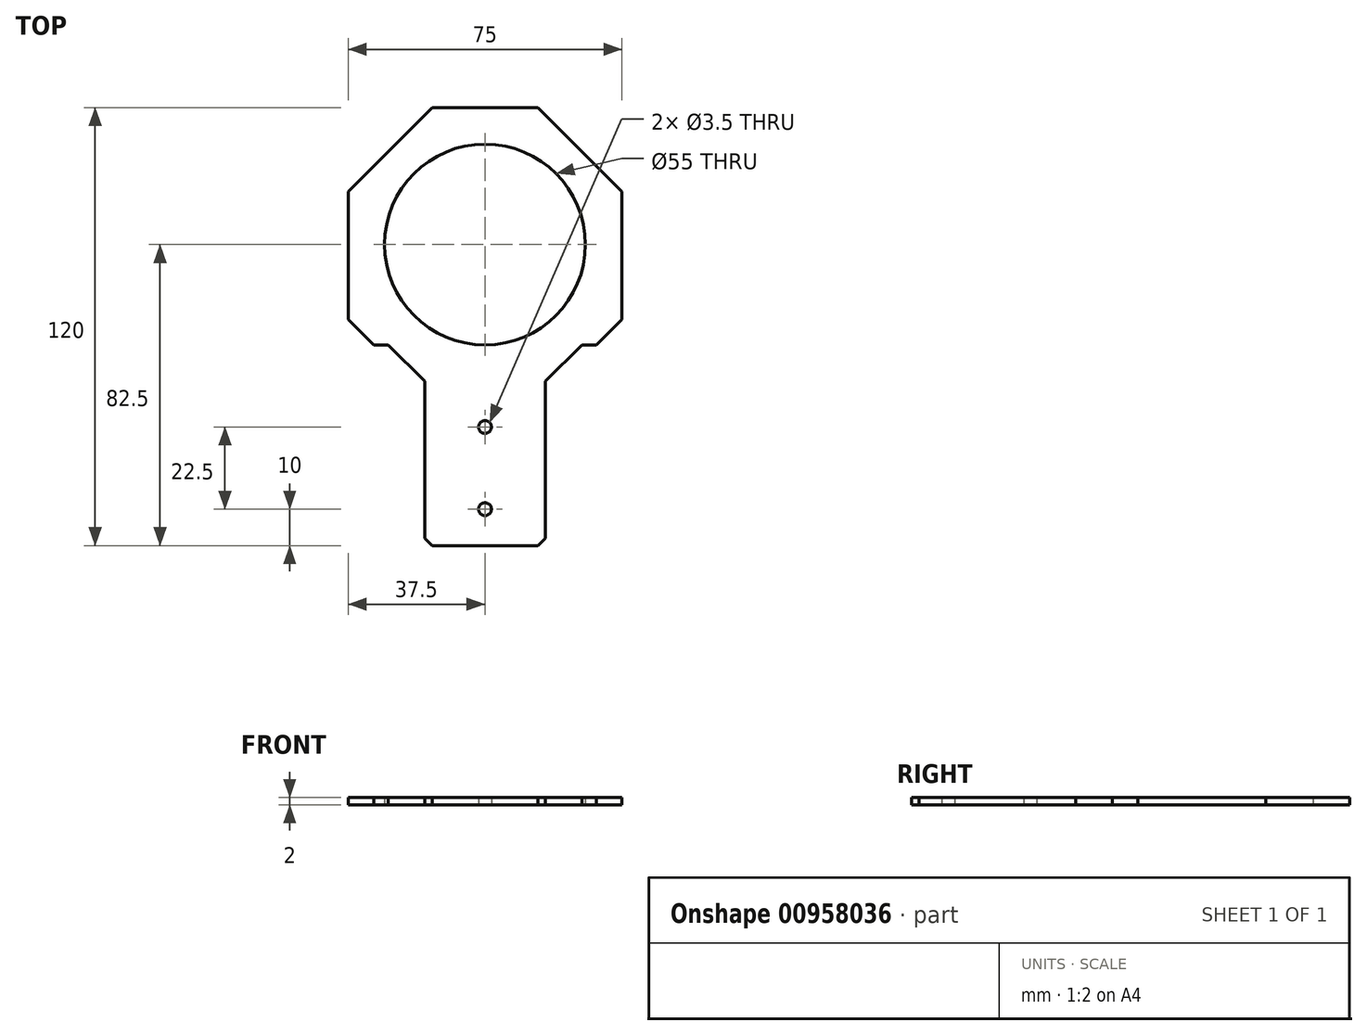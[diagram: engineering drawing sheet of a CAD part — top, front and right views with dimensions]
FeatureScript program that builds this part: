
annotation { "Feature Type Name" : "Feature", "Feature Type Description" : "" }
export const myFeature = defineFeature(function(context is Context, id is Id, definition is map)
    precondition{}
    {
        {
            var Q0;
            Q0=qCreatedBy(makeId("Top.planeOp"),FACE);
            var sketch = newSketch(context, id + "F0", { "sketchPlane" : qUnion([Q0])});
            skCircle(sketch, "E0", {"center": v(0, 0) * mm, "radius": 27.5 * mm});
            skLineSegment(sketch, "E1", {"start": v(0, 37.5) * mm, "end": v(0, 0) * mm, "construction": true});
            skLineSegment(sketch, "E2", {"start": v(0, 0) * mm, "end": v(37.5, 0) * mm, "construction": true});
            skLineSegment(sketch, "E3", {"start": v(0, 37.5) * mm, "end": v(-14.5, 37.5) * mm});
            skLineSegment(sketch, "E4", {"start": v(-14.5, 37.5) * mm, "end": v(-37.5, 14.5) * mm});
            skLineSegment(sketch, "E5", {"start": v(-37.5, 14.5) * mm, "end": v(-37.5, -20.5) * mm});
            skLineSegment(sketch, "E6", {"start": v(-37.5, -20.5) * mm, "end": v(-30.5, -27.5) * mm});
            skLineSegment(sketch, "E7", {"start": v(-30.5, -27.5) * mm, "end": v(-26.5, -27.5) * mm});
            skLineSegment(sketch, "E8", {"start": v(-26.5, -27.5) * mm, "end": v(-16.5, -37.5) * mm});
            skLineSegment(sketch, "E9", {"start": v(-16.5, -37.5) * mm, "end": v(-16.5, -80.5) * mm});
            skLineSegment(sketch, "E10", {"start": v(-16.5, -80.5) * mm, "end": v(-14.5, -82.5) * mm});
            skLineSegment(sketch, "E11", {"start": v(-14.5, -82.5) * mm, "end": v(0, -82.5) * mm});
            skCircle(sketch, "E12", {"center": v(0, -50) * mm, "radius": 1.75 * mm});
            skCircle(sketch, "E13", {"center": v(0, -72.5) * mm, "radius": 1.75 * mm});
            skLineSegment(sketch, "E14.MirrorCS", {"start": v(14.5, -82.5) * mm, "end": v(0, -82.5) * mm});
            skLineSegment(sketch, "E15.MirrorCS", {"start": v(16.5, -80.5) * mm, "end": v(14.5, -82.5) * mm});
            skLineSegment(sketch, "E16.MirrorCS", {"start": v(16.5, -37.5) * mm, "end": v(16.5, -80.5) * mm});
            skLineSegment(sketch, "E17.MirrorCS", {"start": v(26.5, -27.5) * mm, "end": v(16.5, -37.5) * mm});
            skLineSegment(sketch, "E18.MirrorCS", {"start": v(30.5, -27.5) * mm, "end": v(26.5, -27.5) * mm});
            skLineSegment(sketch, "E19.MirrorCS", {"start": v(37.5, -20.5) * mm, "end": v(30.5, -27.5) * mm});
            skLineSegment(sketch, "E20.MirrorCS", {"start": v(37.5, 14.5) * mm, "end": v(37.5, -20.5) * mm});
            skLineSegment(sketch, "E21.MirrorCS", {"start": v(0, 37.5) * mm, "end": v(14.5, 37.5) * mm});
            skLineSegment(sketch, "E22.MirrorCS", {"start": v(14.5, 37.5) * mm, "end": v(37.5, 14.5) * mm});
            skSolve(sketch);
        }
        {
            var Q0;
            Q0 = qSketchRegion(id + "F0", true);
            extrude(context, id + "F1", {"entities" : qUnion([Q0]), "depth" : 2 * mm, "offsetDistance" : 25 * mm});
        }
    });
